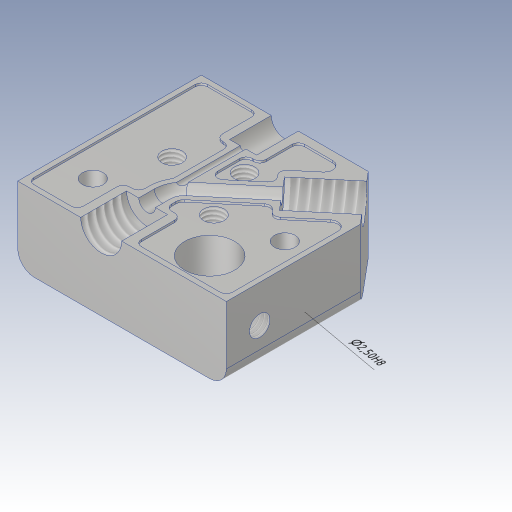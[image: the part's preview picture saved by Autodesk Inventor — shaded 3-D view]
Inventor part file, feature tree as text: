
AUTODESK INVENTOR PART (.ipt)
format: ipt  version: 2023.3 (Build 273359000, 359)  size: 486,912 bytes
history: native  units: in
note: dims shown in document units (in); Inventor stores cm internally (conversion verified against a paired STEP export)
features: sketch x9, hole x9, projected_geometry x7, extrude x3, other x2, sweep x1, revolve x1, fillet x1
ambient origin geometry x8: Origin, YZ Plane, XZ Plane, XY Plane, X Axis, Y Axis, Z Axis, Center Point
bodies: Body1 (feature_tree)
feature tree (33):
  other  "Anmerkungen"
  sketch  "Skizze3"  dims[d115=0.2362in d116=0.2362in]
  extrude  "Extrusion11"  Depth=0.2362in
  sketch  "Skizze19"  dims[d117=0.1575in d234=0.8933in]
  sweep  "Sweeping4"
  hole  "Bohrung17"  [1 undecoded]
  sketch  "Skizze20"  dims[d236=0.9843in d237=0.8661in]
  hole  "Bohrung18"  [1 undecoded]
  hole  "Bohrung27"  [1 undecoded]
  sketch  "Skizze21"  dims[d238=0.0984in d239=0.3543in d240=0.0in]
  hole  "Bohrung20"  [1 undecoded]
  revolve  "Umdrehung2"
  hole  "Bohrung28"  [1 undecoded]
  sketch  "Skizze24"  dims[d252=0.1936in d253=0.1969in d254=0.1575in d255=0.0787in d256=90.0deg d257=0.2165in d258=0.0in]
  hole  "Bohrung23"  [1 undecoded]
  fillet  "Rundung5"  Radius=0.5906in
  hole  "Bohrung24"  [1 undecoded]
  sketch  "Skizze25"  dims[d266=0.1276in d267=0.1575in d268=0.1575in d269=0.0787in d270=90.0deg d271=0.1969in d272=0.0in d273=0.0394in]
  hole  "Bohrung25"  [1 undecoded]
  hole  "Bohrung26"  [1 undecoded]
  extrude  "Extrusion12"  Depth=0.0394in
  extrude  "Extrusion14"  Depth=0.0984in
  sketch  "Skizze22"  dims[d241=0.0787in d243=0.0in d244=0.0in]
  projected_geometry  "Projizierte Kontur1"
  sketch  "Skizze23"  dims[d245=0.1936in d246=0.2559in d247=0.4961in d248=0.2598in d249=90.0deg d250=0.2756in d251=0.0in]
  projected_geometry  "Projizierte Kontur4"
  projected_geometry  "Projizierte Kontur5"
  projected_geometry  "Projizierte Kontur6"
  projected_geometry  "Projizierte Kontur10"
  projected_geometry  "Projizierte Kontur11"
  sketch  "Skizze27"  dims[d274=0.0197in d275=0.1181in d276=360.0deg d299=0.0984in d300=0.315in d301=0.1575in d302=0.0787in d303=90.0deg d304=0.2756in d305=0.0in d306=0.5906in d307=0.0787in d312=0.0968in d313=0.3937in d314=0.1575in d315=0.0787in d316=90.0deg d317=0.2992in d318=0.0in d325=0.7874in d326=0.1575in d327=0.1575in d328=0.0984in d329=0.0984in d330=0.1969in d331=0.1575in d332=0.0787in d333=90.0deg d334=0.1378in d335=0.0in d336=0.0617in d337=0.1181in d338=0.1575in d339=0.0787in d340=90.0deg d341=0.1575in d342=0.8108in d343=0.2874in d344=0.4724in d345=45.0deg d347=0.0276in d348=0.5906in d349=0.0in d350=0.0276in d351=0.2362in d352=0.1575in d353=0.0787in d354=90.0deg d355=0.4331in d356=0.0in d357=0.2559in d358=0.3937in d359=0.1575in d360=0.1969in d361=0.0in d362=360.0deg d363=0.0236in d366=0.0968in d367=0.2362in d368=0.1732in d369=0.0945in d370=0.5635in d371=0.2362in d372=0.8108in d381=0.4913in d382=0.1181in d383=0.3937in d384=0.3346in d400=0.0236in d401=0.0236in d402=0.0394in d403=0.0394in d404=0.0394in d405=0.0236in d406=0.0236in d407=0.0236in d408=0.0236in d409=0.0394in d410=0.0394in d411=0.0394in d412=0.0394in d413=0.0394in d414=0.0295in d415=0.0098in d416=0.0in d321=0.5865in d322=0.2521in d323=-0.1684in d324=0.0984in d398=0.0394in d399=0.0394in]
  projected_geometry  "Projizierte Kontur14"
  other  "Durchmesserbemaßung 1"
note: 9 required parameter values undecoded (feature->parameter linkage not recoverable at this tier; creation-order binding heuristic only, values carry confidence <= 0.55)
